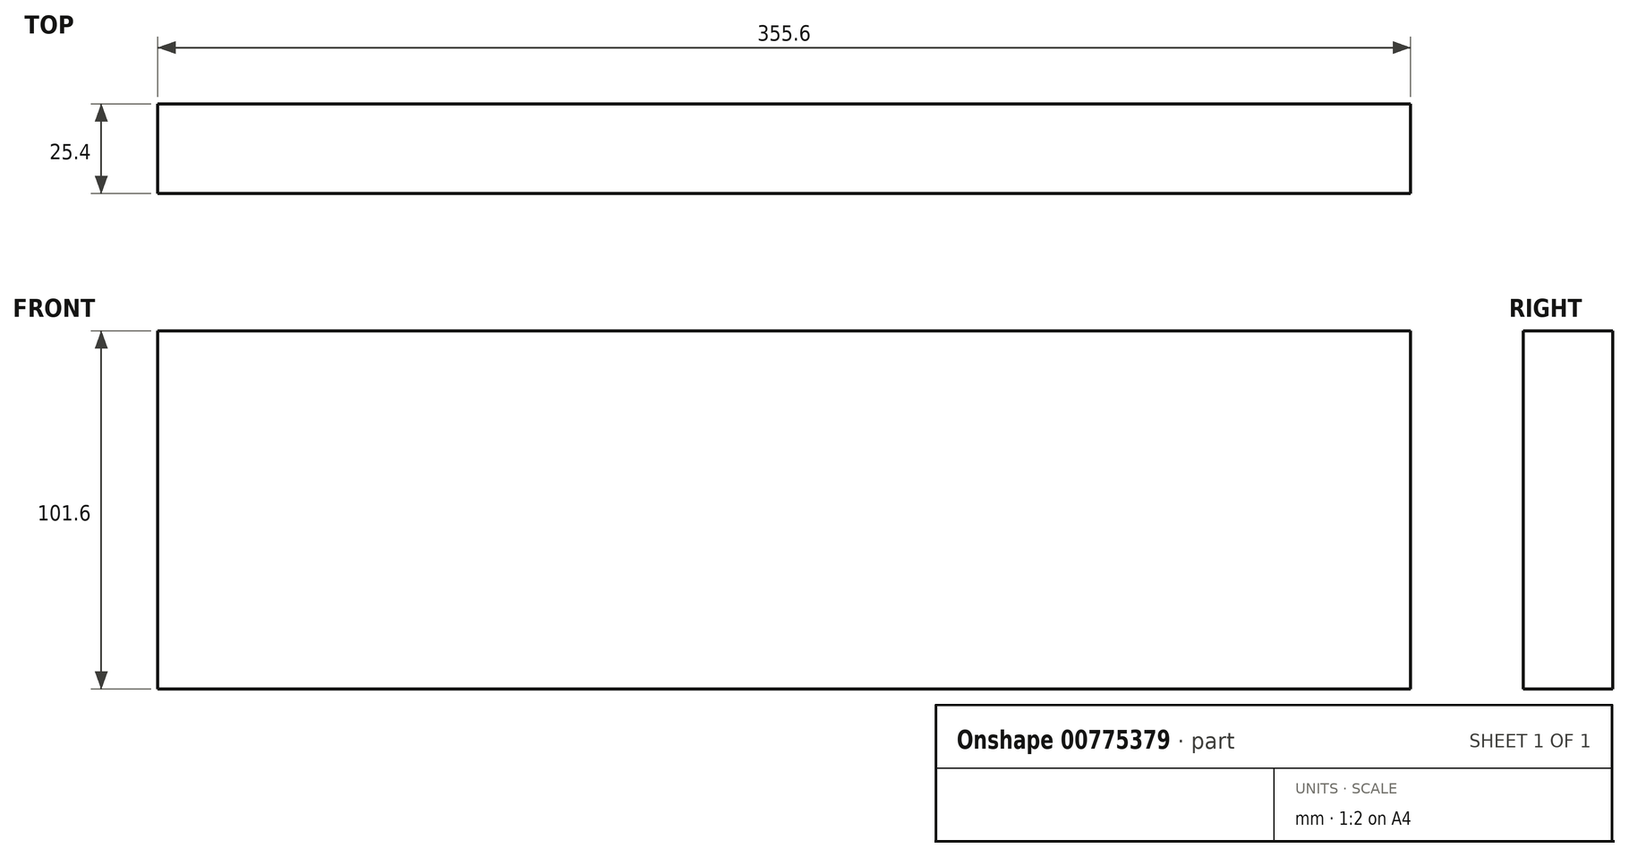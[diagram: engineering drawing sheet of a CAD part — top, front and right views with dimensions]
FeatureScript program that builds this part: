
annotation { "Feature Type Name" : "Feature", "Feature Type Description" : "" }
export const myFeature = defineFeature(function(context is Context, id is Id, definition is map)
    precondition{}
    {
        {
            var Q0;
            Q0=qCreatedBy(makeId("Front.planeOp"),FACE);
            var sketch = newSketch(context, id + "F0", { "sketchPlane" : qUnion([Q0])});
            skLineSegment(sketch, "E0.bottom", {"start": v(-177.8, 50.8) * mm, "end": v(177.8, 50.8) * mm});
            skLineSegment(sketch, "E0.top", {"start": v(-177.8, -50.8) * mm, "end": v(177.8, -50.8) * mm});
            skLineSegment(sketch, "E0.left", {"start": v(-177.8, 50.8) * mm, "end": v(-177.8, -50.8) * mm});
            skLineSegment(sketch, "E0.right", {"start": v(177.8, 50.8) * mm, "end": v(177.8, -50.8) * mm});
            skPoint(sketch, "E0.middle", {"position": v(0, 0) * mm});
            skSolve(sketch);
        }
        {
            var Q0;
            Q0=qSketchRegion(id+"F0",true);
            extrude(context, id + "F1", {"entities" : qUnion([Q0]), "endBound" : BoundingType.SYMMETRIC, "depth" : 25.4 * mm, "offsetDistance" : 25.4 * mm});
        }
    });
